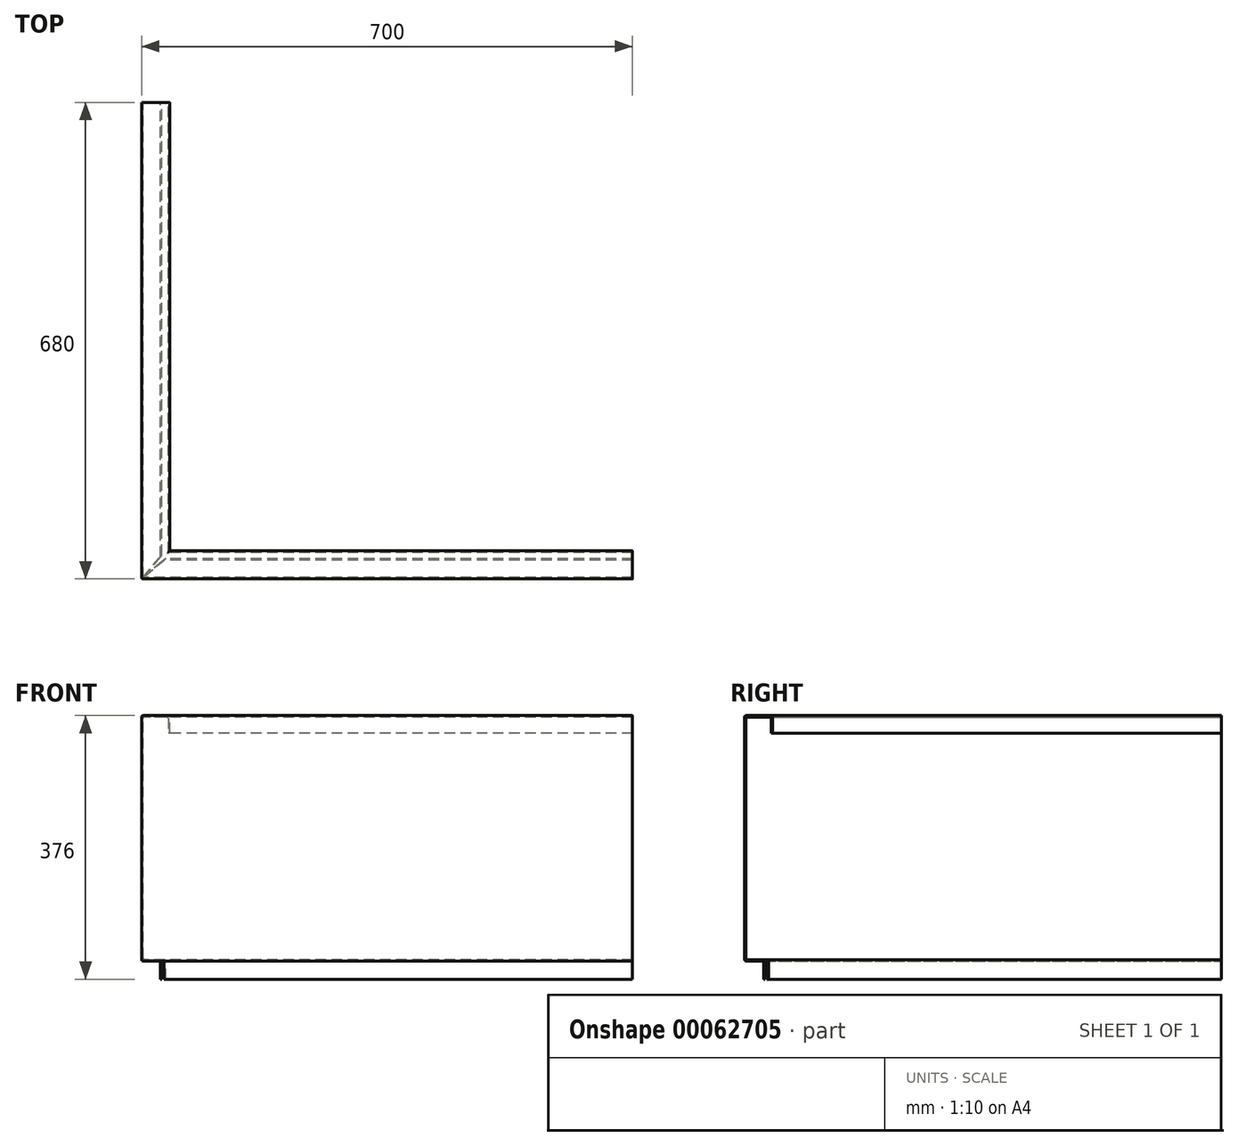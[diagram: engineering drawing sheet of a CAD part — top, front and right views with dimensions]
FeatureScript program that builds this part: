
annotation { "Feature Type Name" : "Feature", "Feature Type Description" : "" }
export const myFeature = defineFeature(function(context is Context, id is Id, definition is map)
    precondition{}
    {
        {
            var Q0;
            Q0=qCreatedBy(makeId("Right.planeOp"),FACE);
            var sketch = newSketch(context, id + "F0", { "sketchPlane" : qUnion([Q0])});
            skLineSegment(sketch, "E0.0", {"start": v(0, -350) * mm, "end": v(27, -350) * mm});
            skLineSegment(sketch, "E0.1", {"start": v(0, 0) * mm, "end": v(0, -350) * mm});
            skLineSegment(sketch, "E1", {"start": v(2, -348) * mm, "end": v(29, -348) * mm});
            skLineSegment(sketch, "E2", {"start": v(2, -2) * mm, "end": v(2, -348) * mm});
            skLineSegment(sketch, "E3", {"start": v(38, -2) * mm, "end": v(2, -2) * mm});
            skLineSegment(sketch, "E4", {"start": v(38, -25) * mm, "end": v(38, -2) * mm});
            skLineSegment(sketch, "E5", {"start": v(27, -350) * mm, "end": v(27, -376) * mm});
            skLineSegment(sketch, "E6", {"start": v(29, -348) * mm, "end": v(29, -376) * mm});
            skLineSegment(sketch, "E0.2", {"start": v(40, 0) * mm, "end": v(0, 0) * mm});
            skLineSegment(sketch, "E0.3", {"start": v(40, -25) * mm, "end": v(40, 0) * mm});
            skLineSegment(sketch, "E7", {"start": v(40, -25) * mm, "end": v(38, -25) * mm});
            skLineSegment(sketch, "E8", {"start": v(29, -376) * mm, "end": v(27, -376) * mm});
            skSolve(sketch);
        }
        {
            var Q0;
            Q0=qCreatedBy(makeId("Top.planeOp"),FACE);
            var sketch = newSketch(context, id + "F1", { "sketchPlane" : qUnion([Q0])});
            skLineSegment(sketch, "E9", {"start": v(0, 0) * mm, "end": v(-700, 0) * mm});
            skLineSegment(sketch, "E10", {"start": v(-700, 0) * mm, "end": v(-700, 680) * mm});
            skSolve(sketch);
        }
        {
            var Q0;
            Q0 = qSketchRegion(id + "F0", true);
            var Q1;
            Q1 = qConstructionFilter(qBodyType(qCreatedBy(id + "F1" ,EDGE), BodyType.WIRE), ConstructionObject.NO);
            sweep(context, id + "F2", {"profiles" : qUnion([Q0]), "path" : qUnion([Q1])});
        }
        {
            var Q0;
            Q0=makeQuery(id+"F2.opSweep","SWEPT_FACE",FACE,{"disambiguationData":[OSD([sQuery(id+"F0.wireOp",EDGE,"E1"),sQuery(id+"F1.wireOp",EDGE,"E9")])]});
            var sketch = newSketch(context, id + "F3", { "sketchPlane" : qUnion([Q0])});
            skLineSegment(sketch, "E11", {"start": v(-698, 2) * mm, "end": v(-665.82, 29) * mm});
            skLineSegment(sketch, "E12", {"start": v(-665.82, 29) * mm, "end": v(-671, 29) * mm});
            skLineSegment(sketch, "E13", {"start": v(-671, 29) * mm, "end": v(-671, 34.18) * mm});
            skLineSegment(sketch, "E14", {"start": v(-671, 34.18) * mm, "end": v(-698, 2) * mm});
            skSolve(sketch);
        }
        {
            var Q0;
            Q0 = qSketchRegion(id + "F3", true);
            extrude(context, id + "F4", {"entities" : qUnion([Q0]), "operationType" : NewBodyOperationType.REMOVE, "oppositeDirection" : true, "depth" : 30 * mm});
        }
        {
            var Q0;
            Q0=makeQuery(id+"F2.opSweep","SWEPT_EDGE",EDGE,{"disambiguationData":[OSD([sQuery(id+"F0.wireOp",EDGE,"E0.2"),sQuery(id+"F0.wireOp",EDGE,"E0.3"),sQuery(id+"F1.wireOp",EDGE,"E10")])]});
            var Q1;
            Q1=makeQuery(id+"F2.opSweep","SWEPT_EDGE",EDGE,{"disambiguationData":[OSD([sQuery(id+"F0.wireOp",EDGE,"E0.2"),sQuery(id+"F0.wireOp",EDGE,"E0.3"),sQuery(id+"F1.wireOp",EDGE,"E9")])]});
            var Q2;
            Q2=makeQuery(id+"F2.opSweep","SWEPT_EDGE",EDGE,{"disambiguationData":[OSD([sQuery(id+"F0.wireOp",EDGE,"E0.1"),sQuery(id+"F0.wireOp",EDGE,"E0.2"),sQuery(id+"F1.wireOp",EDGE,"E10")])]});
            var Q3;
            Q3=makeQuery(id+"F2.opSweep","SWEPT_EDGE",EDGE,{"disambiguationData":[OSD([sQuery(id+"F0.wireOp",EDGE,"E0.1"),sQuery(id+"F0.wireOp",EDGE,"E0.2"),sQuery(id+"F1.wireOp",EDGE,"E9")])]});
            var Q4;
            Q4=makeQuery(id+"F2.opSweep","SWEPT_EDGE",EDGE,{"disambiguationData":[OSD([sQuery(id+"F0.wireOp",EDGE,"E0.0"),sQuery(id+"F0.wireOp",EDGE,"E0.1"),sQuery(id+"F1.wireOp",EDGE,"E9")])]});
            var Q5;
            Q5=makeQuery(id+"F2.opSweep","SWEPT_EDGE",EDGE,{"disambiguationData":[OSD([sQuery(id+"F0.wireOp",EDGE,"E0.0"),sQuery(id+"F0.wireOp",EDGE,"E5"),sQuery(id+"F1.wireOp",EDGE,"E9")])]});
            var Q6;
            Q6=makeQuery(id+"F2.opSweep","SWEPT_EDGE",EDGE,{"disambiguationData":[OSD([sQuery(id+"F0.wireOp",EDGE,"E0.0"),sQuery(id+"F0.wireOp",EDGE,"E0.1"),sQuery(id+"F1.wireOp",EDGE,"E10")])]});
            var Q7;
            Q7=makeQuery(id+"F2.opSweep","SWEPT_EDGE",EDGE,{"disambiguationData":[OSD([sQuery(id+"F0.wireOp",EDGE,"E0.0"),sQuery(id+"F0.wireOp",EDGE,"E5"),sQuery(id+"F1.wireOp",EDGE,"E10")])]});
            var Q8;
            Q8=makeQuery(id+"F2.opSweep","MID_CAP_EDGE",EDGE,{"disambiguationData":[OSD([sQuery(id+"F0.wireOp",EDGE,"E0.1"),sQuery(id+"F1.wireOp",VERTEX,"E10.start")])],"capPos":1.0});
            var Q9;
            Q9=makeQuery(id+"F2.opSweep","SWEPT_EDGE",EDGE,{"disambiguationData":[OSD([sQuery(id+"F0.wireOp",EDGE,"E1"),sQuery(id+"F0.wireOp",EDGE,"E6"),sQuery(id+"F1.wireOp",EDGE,"E10")])]});
            var Q10;
            Q10=makeQuery(id+"F2.opSweep","SWEPT_EDGE",EDGE,{"disambiguationData":[OSD([sQuery(id+"F0.wireOp",EDGE,"E1"),sQuery(id+"F0.wireOp",EDGE,"E2"),sQuery(id+"F1.wireOp",EDGE,"E10")])]});
            var Q11;
            Q11=makeQuery(id+"F2.opSweep","SWEPT_EDGE",EDGE,{"disambiguationData":[OSD([sQuery(id+"F0.wireOp",EDGE,"E1"),sQuery(id+"F0.wireOp",EDGE,"E6"),sQuery(id+"F1.wireOp",EDGE,"E9")])]});
            var Q12;
            Q12=makeQuery(id+"F2.opSweep","SWEPT_EDGE",EDGE,{"disambiguationData":[OSD([sQuery(id+"F0.wireOp",EDGE,"E1"),sQuery(id+"F0.wireOp",EDGE,"E2"),sQuery(id+"F1.wireOp",EDGE,"E9")])]});
            var Q13;
            Q13=makeQuery(id+"F2.opSweep","SWEPT_EDGE",EDGE,{"disambiguationData":[OSD([sQuery(id+"F0.wireOp",EDGE,"E2"),sQuery(id+"F0.wireOp",EDGE,"E3"),sQuery(id+"F1.wireOp",EDGE,"E9")])]});
            var Q14;
            Q14=makeQuery(id+"F2.opSweep","SWEPT_EDGE",EDGE,{"disambiguationData":[OSD([sQuery(id+"F0.wireOp",EDGE,"E2"),sQuery(id+"F0.wireOp",EDGE,"E3"),sQuery(id+"F1.wireOp",EDGE,"E10")])]});
            var Q15;
            Q15=makeQuery(id+"F2.opSweep","SWEPT_EDGE",EDGE,{"disambiguationData":[OSD([sQuery(id+"F0.wireOp",EDGE,"E3"),sQuery(id+"F0.wireOp",EDGE,"E4"),sQuery(id+"F1.wireOp",EDGE,"E10")])]});
            var Q16;
            Q16=makeQuery(id+"F2.opSweep","SWEPT_EDGE",EDGE,{"disambiguationData":[OSD([sQuery(id+"F0.wireOp",EDGE,"E3"),sQuery(id+"F0.wireOp",EDGE,"E4"),sQuery(id+"F1.wireOp",EDGE,"E9")])]});
            fillet(context, id + "F5", {"entities" : qUnion([Q0, Q1, Q2, Q3, Q4, Q5, Q6, Q7, Q8, Q9, Q10, Q11, Q12, Q13, Q14, Q15, Q16]), "radius" : 2 * mm, "tangentPropagation" : true, "allowEdgeOverflow" : false});
        }
    });
